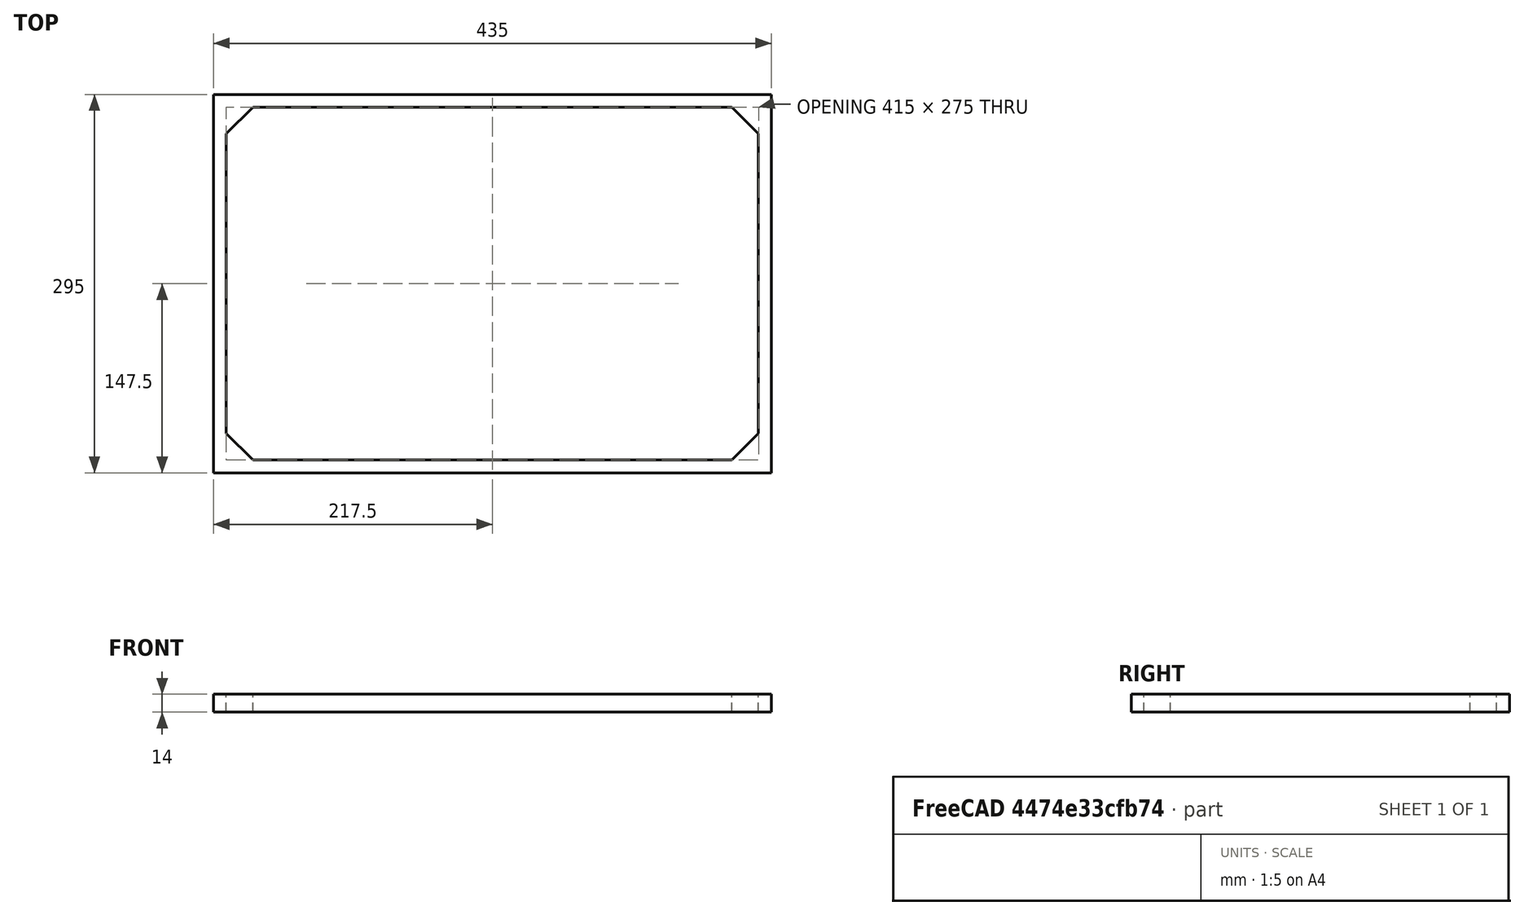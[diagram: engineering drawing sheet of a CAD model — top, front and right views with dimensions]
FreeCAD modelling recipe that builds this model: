
FCSTD DOCUMENT  (FreeCAD 0.20R29603 (Git))
Label: Glasrahmen-Fenster_Doppelglas_440x300
License: All rights reserved
LicenseURL: http://en.wikipedia.org/wiki/All_rights_reserved
objects: Sketcher::SketchObject×1, PartDesign::Pad×1, PartDesign::Body×1
note: 4 computed .brp shape members not serialized (recipe doc carries the construction recipe); baked Part::Feature solids carry a one-line shape summary decoded from their .brp

FEATURE [Sketcher::SketchObject] Sketch
  FullyConstrained = true
  MapMode = 5
  Support = -> [XY_Plane]
  sketch-geometry (13):
    g0: LineSegment StartX=-217.5 StartY=147.5 StartZ=0 EndX=-217.5 EndY=-147.5 EndZ=0
    g1: LineSegment StartX=-217.5 StartY=-147.5 StartZ=0 EndX=217.5 EndY=-147.5 EndZ=0
    g2: LineSegment StartX=217.5 StartY=-147.5 StartZ=0 EndX=217.5 EndY=147.5 EndZ=0
    g3: LineSegment StartX=217.5 StartY=147.5 StartZ=0 EndX=-217.5 EndY=147.5 EndZ=0
    g4: GeomPoint X=0 Y=0 Z=0
    g5: LineSegment StartX=186.789 StartY=-137.5 StartZ=0 EndX=-186.789 EndY=-137.5 EndZ=0
    g6: LineSegment StartX=-186.789 StartY=-137.5 StartZ=0 EndX=-207.5 EndY=-116.789 EndZ=0
    g7: LineSegment StartX=-207.5 StartY=-116.789 StartZ=0 EndX=-207.5 EndY=116.789 EndZ=0
    g8: LineSegment StartX=-207.5 StartY=116.789 StartZ=0 EndX=-186.789 EndY=137.5 EndZ=0
    g9: LineSegment StartX=-186.789 StartY=137.5 StartZ=0 EndX=186.789 EndY=137.5 EndZ=0
    g10: LineSegment StartX=186.789 StartY=137.5 StartZ=0 EndX=207.5 EndY=116.789 EndZ=0
    g11: LineSegment StartX=207.5 StartY=116.789 StartZ=0 EndX=207.5 EndY=-116.789 EndZ=0
    g12: LineSegment StartX=207.5 StartY=-116.789 StartZ=0 EndX=186.789 EndY=-137.5 EndZ=0
  constraints (32):
    c: Coincident(g0,g1)
    c: Coincident(g1,g2)
    c: Coincident(g2,g3)
    c: Coincident(g3,g0)
    c: Horizontal(g1)
    c: Horizontal(g3)
    c: Vertical(g0)
    c: Vertical(g2)
    c: Symmetric(g1,g0,g4)
    c: Coincident(g4,g-1)
    c: Distance(g1) = 435
    c: Distance(g2) = 295
    c: Coincident(g5,g6)
    c: Coincident(g6,g7)
    c: Vertical(g7)
    c: Coincident(g7,g8)
    c: Coincident(g8,g9)
    c: Coincident(g9,g10)
    c: Coincident(g10,g11)
    c: Vertical(g11)
    c: Coincident(g11,g12)
    c: Coincident(g12,g5)
    c: Symmetric(g10,g7,g-2)
    c: Symmetric(g5,g8,g-1)
    c: Distance(g10,g2) = 10
    c: Distance(g9,g3) = 10
    c: Equal(g10,g12)
    c: Equal(g12,g6)
    c: Angle(g6,g7) = 2.35619
    c: Symmetric(g5,g5,g-2)
    c: Symmetric(g9,g8,g-2)
    c: Distance(g12) = 29.29
FEATURE [PartDesign::Pad] Pad
  Direction = (0,0,1)
  Length = 14
  Length2 = 10
  Profile = -> Sketch
  ReferenceAxis = -> Sketch [N_Axis]
  Type = 0
FEATURE [PartDesign::Body] Body
  Group = -> [Sketch,Pad]
  Origin = -> Origin
  Tip = -> Pad
